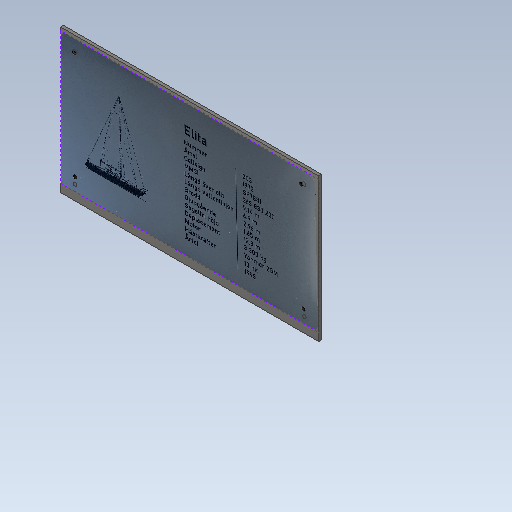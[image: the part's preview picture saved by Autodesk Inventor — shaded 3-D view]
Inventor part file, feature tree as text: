
AUTODESK INVENTOR PART (.ipt)
format: ipt  version: 2021 (Build 250183000, 183)  size: 3,802,624 bytes
history: native  units: mm
features: sketch x3, extrude x2, other x1
ambient origin geometry x8: Origin, YZ Plane, XZ Plane, XY Plane, X Axis, Y Axis, Z Axis, Center Point
bodies: Solid1 (feature_tree)
feature tree (6):
  extrude  "Extrusion1"  Depth=100.0mm
  sketch  "Sketch2"  dims[d2=2.0mm d3=0.0mm d21=2.5mm]
  extrude  "Extrusion2"  Depth=2.0mm
  sketch  "Sketch1"  dims[d0=180.0mm d1=100.0mm]
  other  "Image1"
  sketch  "Sketch3"  dims[d23=10.0mm d24=10.0mm d25=2.0mm d26=0.0mm]
